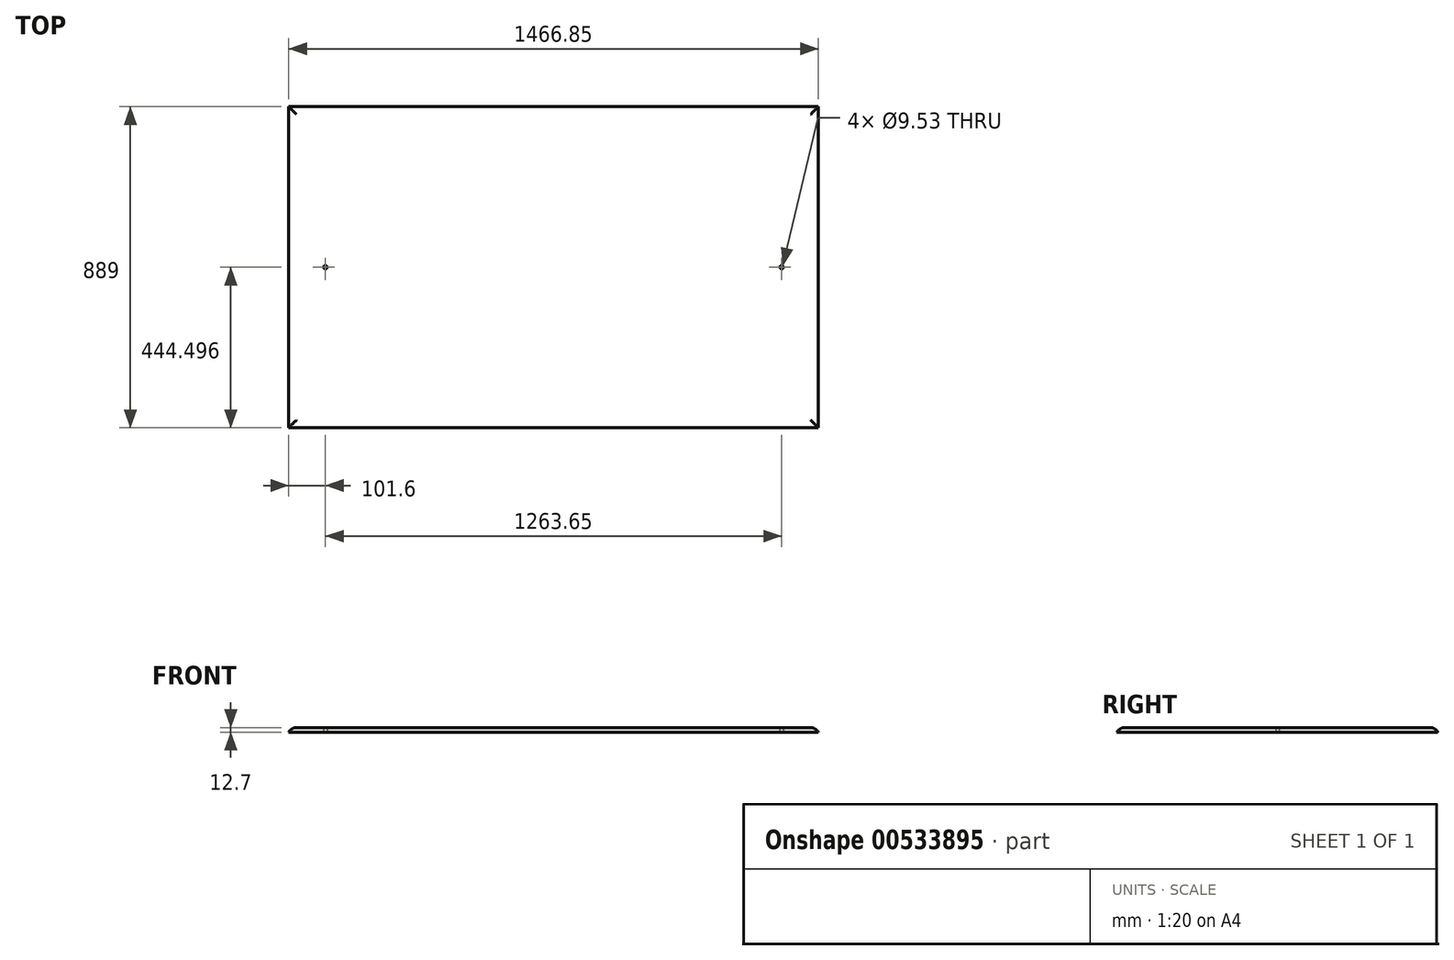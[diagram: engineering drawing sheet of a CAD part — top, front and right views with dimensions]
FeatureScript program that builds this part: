
annotation { "Feature Type Name" : "Feature", "Feature Type Description" : "" }
export const myFeature = defineFeature(function(context is Context, id is Id, definition is map)
    precondition{}
    {
        {
            var Q0;
            Q0=qCreatedBy(makeId("Top.planeOp"),FACE);
            var sketch = newSketch(context, id + "F0", { "sketchPlane" : qUnion([Q0])});
            skLineSegment(sketch, "E0", {"start": v(-101.6, -76.17) * mm, "end": v(1365.25, -76.17) * mm});
            skLineSegment(sketch, "E1", {"start": v(-101.6, -76.17) * mm, "end": v(-101.6, 812.83) * mm});
            skLineSegment(sketch, "E2", {"start": v(-101.6, 812.83) * mm, "end": v(1365.25, 812.83) * mm});
            skLineSegment(sketch, "E3", {"start": v(1365.25, 812.83) * mm, "end": v(1365.25, -76.17) * mm});
            skPoint(sketch, "E4.orphan", {"position": v(-101.6, 368.33) * mm});
            skPoint(sketch, "E5.orphan", {"position": v(-69.85, -76.17) * mm});
            skPoint(sketch, "E6.end.orphan", {"position": v(-69.85, 812.83) * mm});
            skPoint(sketch, "E7.orphan", {"position": v(1365.25, 368.33) * mm});
            skLineSegment(sketch, "E8", {"start": v(1365.25, 812.83) * mm, "end": v(1365.25, 736.63) * mm});
            skPoint(sketch, "E9.orphan", {"position": v(-101.6, 736.63) * mm});
            skPoint(sketch, "E10.orphan", {"position": v(-101.6, 0.03) * mm});
            skPoint(sketch, "E11.center.orphan", {"position": v(1339.85, 0) * mm});
            skPoint(sketch, "E12.start.orphan", {"position": v(1365.25, 0) * mm});
            skLineSegment(sketch, "E13.bottom", {"start": v(-76.2, 787.43) * mm, "end": v(1339.85, 787.43) * mm});
            skLineSegment(sketch, "E13.top", {"start": v(-76.2, -50.77) * mm, "end": v(1339.85, -50.77) * mm});
            skLineSegment(sketch, "E13.left", {"start": v(-76.2, 787.43) * mm, "end": v(-76.2, -50.77) * mm});
            skLineSegment(sketch, "E13.right", {"start": v(1339.85, 787.43) * mm, "end": v(1339.85, -50.77) * mm});
            skPoint(sketch, "E13.middle", {"position": v(631.82, 368.33) * mm});
            skPoint(sketch, "E13.middle.positionSnap0", {"position": v(631.82, 812.83) * mm});
            skPoint(sketch, "E13.centerSnap0", {"position": v(631.82, 812.83) * mm});
            skPoint(sketch, "E14.center.orphan", {"position": v(-69.85, 368.33) * mm});
            skPoint(sketch, "E15.center.orphan", {"position": v(1314.45, 0) * mm});
            skCircle(sketch, "E16", {"center": v(0, 368.33) * mm, "radius": 4.76 * mm});
            skPoint(sketch, "E17.orphan", {"position": v(0, 787.43) * mm});
            skPoint(sketch, "E18.orphan", {"position": v(0, -50.77) * mm});
            skCircle(sketch, "E19", {"center": v(1263.65, 368.33) * mm, "radius": 4.76 * mm});
            skSolve(sketch);
        }
        {
            var Q0;
            Q0=makeQuery(id+"F0.imprint","IMPRINT",FACE,{"disambiguationData":[TD([[makeQuery(id+"F0.imprint","IMPRINT",EDGE,{"derivedFrom":sQuery(id+"F0.wireOp",EDGE,"E6S8cBOx-WbZ9-htJr-9T32-4TB8pj6YNGIc")}),1.0]])]});
            var Q1;
            {var subQ0=sQuery(id+"F0.wireOp",EDGE,"TDuMDo8L-DCFb-70Zj-w6wx-SX7NcPyYi2b4");var subQ1=sQuery(id+"F0.wireOp",EDGE,"E0");var subQ2=makeQuery(id+"F0.imprint","INTERSECT",VERTEX,{"disambiguationData":[OD(0.0)],"derivedFrom":[subQ1,subQ0]});Q1=makeQuery(id+"F0.imprint","IMPRINT",FACE,{"disambiguationData":[TD([[makeQuery(id+"F0.imprint","IMPRINT",EDGE,{"disambiguationData":[TD([[subQ2,-1.0]])],"derivedFrom":subQ1}),-1.0]])]});}
            var Q2;
            {var subQ0=sQuery(id+"F0.wireOp",EDGE,"TDuMDo8L-DCFb-70Zj-w6wx-SX7NcPyYi2b4");var subQ1=sQuery(id+"F0.wireOp",EDGE,"E0");var subQ2=makeQuery(id+"F0.imprint","INTERSECT",VERTEX,{"disambiguationData":[OD(0.0)],"derivedFrom":[subQ1,subQ0]});Q2=makeQuery(id+"F0.imprint","IMPRINT",FACE,{"disambiguationData":[TD([[makeQuery(id+"F0.imprint","IMPRINT",EDGE,{"disambiguationData":[TD([[subQ2,-1.0]])],"derivedFrom":subQ1}),1.0]])]});}
            var Q3;
            Q3=makeQuery(id+"F0.imprint","IMPRINT",FACE,{"disambiguationData":[TD([[makeQuery(id+"F0.imprint","IMPRINT",EDGE,{"derivedFrom":sQuery(id+"F0.wireOp",EDGE,"E14")}),-1.0]])]});
            var Q4;
            {var subQ5=sQuery(id+"F0.wireOp",EDGE,"E1");Q4=makeQuery(id+"F0.imprint","IMPRINT",FACE,{"disambiguationData":[TD([[makeQuery(id+"F0.imprint","IMPRINT",EDGE,{"derivedFrom":subQ5}),-1.0]])]});}
            var Q5;
            Q5=makeQuery(id+"F0.imprint","IMPRINT",FACE,{"disambiguationData":[TD([[makeQuery(id+"F0.imprint","IMPRINT",EDGE,{"derivedFrom":sQuery(id+"F0.wireOp",EDGE,"E13.bottom")}),-1.0]])]});
            extrude(context, id + "F1", {"entities" : qUnion([Q0, Q1, Q2, Q3, Q4, Q5]), "depth" : 12.7 * mm, "offsetDistance" : 25.4 * mm});
        }
        {
            var Q0;
            Q0=makeQuery(id+"F1.opExtrude","CAP_EDGE",EDGE,{"disambiguationData":[OSD([sQuery(id+"F0.wireOp",EDGE,"E0")])],"isStart":false});
            var Q1;
            Q1=makeQuery(id+"F1.opExtrude","CAP_EDGE",EDGE,{"disambiguationData":[OSD([sQuery(id+"F0.wireOp",EDGE,"E1")])],"isStart":false});
            var Q2;
            Q2=makeQuery(id+"F1.opExtrude","CAP_EDGE",EDGE,{"disambiguationData":[OSD([sQuery(id+"F0.wireOp",EDGE,"E2")])],"isStart":false});
            var Q3;
            Q3=makeQuery(id+"F1.opExtrude","CAP_EDGE",EDGE,{"disambiguationData":[OSD([sQuery(id+"F0.wireOp",EDGE,"E3"),sQuery(id+"F0.wireOp",EDGE,"E8")])],"isStart":false});
            fillet(context, id + "F2", {"entities" : qUnion([Q0, Q1, Q2, Q3]), "radius" : 25.4 * mm, "tangentPropagation" : true, "allowEdgeOverflow" : false});
        }
    });
